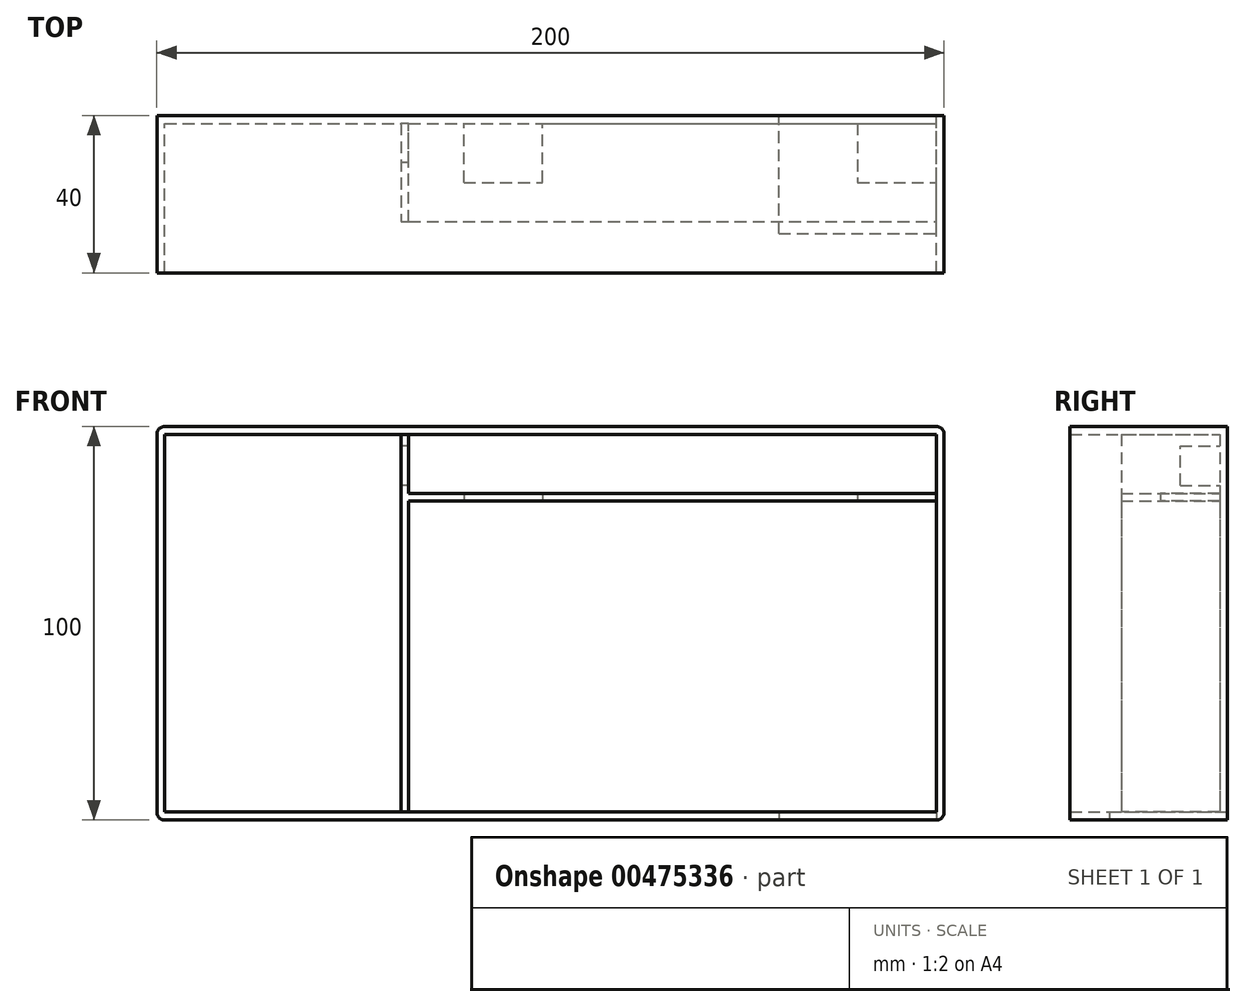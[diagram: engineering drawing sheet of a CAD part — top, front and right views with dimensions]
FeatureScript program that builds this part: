
annotation { "Feature Type Name" : "Feature", "Feature Type Description" : "" }
export const myFeature = defineFeature(function(context is Context, id is Id, definition is map)
    precondition{}
    {
        {
            var Q0;
            Q0=qCreatedBy(makeId("Front.planeOp"),FACE);
            var sketch = newSketch(context, id + "F0", { "sketchPlane" : qUnion([Q0])});
            skLineSegment(sketch, "E0.bottom", {"start": v(-123.67, 31.9) * mm, "end": v(76.33, 31.9) * mm});
            skLineSegment(sketch, "E0.top", {"start": v(-123.67, -68.1) * mm, "end": v(76.33, -68.1) * mm});
            skLineSegment(sketch, "E0.left", {"start": v(-123.67, 31.9) * mm, "end": v(-123.67, -68.1) * mm});
            skLineSegment(sketch, "E0.right", {"start": v(76.33, 31.9) * mm, "end": v(76.33, -68.1) * mm});
            skLineSegment(sketch, "E1.bottom", {"start": v(-121.67, 29.9) * mm, "end": v(74.33, 29.9) * mm});
            skLineSegment(sketch, "E1.top", {"start": v(-121.67, -66.1) * mm, "end": v(74.33, -66.1) * mm});
            skLineSegment(sketch, "E1.left", {"start": v(-121.67, 29.9) * mm, "end": v(-121.67, -66.1) * mm});
            skLineSegment(sketch, "E1.right", {"start": v(74.33, 29.9) * mm, "end": v(74.33, -66.1) * mm});
            skSolve(sketch);
        }
        {
            var Q0;
            Q0=makeQuery(id+"F0.imprint","IMPRINT",FACE,{"disambiguationData":[TD([[makeQuery(id+"F0.imprint","IMPRINT",EDGE,{"derivedFrom":sQuery(id+"F0.wireOp",EDGE,"E0.bottom")}),-1.0]])]});
            extrude(context, id + "F1", {"entities" : qUnion([Q0]), "depth" : 40 * mm});
        }
        {
            var Q0;
            Q0=makeQuery(id+"F0.imprint","IMPRINT",FACE,{"disambiguationData":[TD([[makeQuery(id+"F0.imprint","IMPRINT",EDGE,{"derivedFrom":sQuery(id+"F0.wireOp",EDGE,"E1.bottom")}),-1.0]])]});
            extrude(context, id + "F2", {"entities" : qUnion([Q0]), "operationType" : NewBodyOperationType.ADD, "depth" : 2 * mm});
        }
        {
            var Q0;
            Q0=makeQuery(id+"F2.opExtrude","CAP_FACE",FACE,{"disambiguationData":[OSD([sQuery(id+"F0.wireOp",EDGE,"E1.bottom"),sQuery(id+"F0.wireOp",EDGE,"E1.top"),sQuery(id+"F0.wireOp",EDGE,"E1.left"),sQuery(id+"F0.wireOp",EDGE,"E1.right")])],"isStart":false});
            var sketch = newSketch(context, id + "F3", { "sketchPlane" : qUnion([Q0])});
            skLineSegment(sketch, "E2.bottom", {"start": v(-121.67, 29.9) * mm, "end": v(-59.67, 29.9) * mm});
            skLineSegment(sketch, "E2.top", {"start": v(-121.67, -66.1) * mm, "end": v(-59.67, -66.1) * mm});
            skLineSegment(sketch, "E2.left", {"start": v(-121.67, 29.9) * mm, "end": v(-121.67, -66.1) * mm});
            skLineSegment(sketch, "E2.right", {"start": v(-59.67, 29.9) * mm, "end": v(-59.67, -66.1) * mm});
            skSolve(sketch);
        }
        {
            var Q0;
            Q0 = qSketchRegion(id + "F3", true);
            extrude(context, id + "F4", {"entities" : qUnion([Q0]), "operationType" : NewBodyOperationType.ADD, "depth" : 25 * mm});
        }
        {
            var Q0;
            Q0=makeQuery(id+"F4.opExtrude","CAP_FACE",FACE,{"disambiguationData":[OSD([sQuery(id+"F3.wireOp",EDGE,"E2.bottom"),sQuery(id+"F3.wireOp",EDGE,"E2.top"),sQuery(id+"F3.wireOp",EDGE,"E2.left"),sQuery(id+"F3.wireOp",EDGE,"E2.right")])],"isStart":false});
            var sketch = newSketch(context, id + "F5", { "sketchPlane" : qUnion([Q0])});
            skLineSegment(sketch, "E3.bottom", {"start": v(-121.67, 29.9) * mm, "end": v(-61.67, 29.9) * mm});
            skLineSegment(sketch, "E3.top", {"start": v(-121.67, -66.1) * mm, "end": v(-61.67, -66.1) * mm});
            skLineSegment(sketch, "E3.left", {"start": v(-121.67, 29.9) * mm, "end": v(-121.67, -66.1) * mm});
            skLineSegment(sketch, "E3.right", {"start": v(-61.67, 29.9) * mm, "end": v(-61.67, -66.1) * mm});
            skSolve(sketch);
        }
        {
            var Q0;
            Q0 = qSketchRegion(id + "F5", true);
            extrude(context, id + "F6", {"entities" : qUnion([Q0]), "operationType" : NewBodyOperationType.REMOVE, "oppositeDirection" : true, "depth" : 25 * mm});
        }
        {
            var Q0;
            Q0=makeQuery(id+"F2.opExtrude","CAP_FACE",FACE,{"disambiguationData":[OSD([sQuery(id+"F0.wireOp",EDGE,"E1.bottom"),sQuery(id+"F0.wireOp",EDGE,"E1.top"),sQuery(id+"F0.wireOp",EDGE,"E1.left"),sQuery(id+"F0.wireOp",EDGE,"E1.right")])],"isStart":false});
            var sketch = newSketch(context, id + "F7", { "sketchPlane" : qUnion([Q0])});
            skLineSegment(sketch, "E4.bottom", {"start": v(-59.67, 29.9) * mm, "end": v(-13.67, 29.9) * mm});
            skLineSegment(sketch, "E4.top", {"start": v(-59.67, 14.9) * mm, "end": v(-13.67, 14.9) * mm});
            skLineSegment(sketch, "E4.left", {"start": v(-59.67, 29.9) * mm, "end": v(-59.67, 14.9) * mm});
            skLineSegment(sketch, "E4.right", {"start": v(-13.67, 29.9) * mm, "end": v(-13.67, 14.9) * mm});
            skLineSegment(sketch, "E5.bottom", {"start": v(-61.67, 29.9) * mm, "end": v(-11.67, 29.9) * mm});
            skLineSegment(sketch, "E5.top", {"start": v(-61.67, 12.9) * mm, "end": v(-11.67, 12.9) * mm});
            skLineSegment(sketch, "E5.left", {"start": v(-61.67, 29.9) * mm, "end": v(-61.67, 12.9) * mm});
            skLineSegment(sketch, "E5.right", {"start": v(-11.67, 29.9) * mm, "end": v(-11.67, 12.9) * mm});
            skSolve(sketch);
        }
        {
            var Q0;
            Q0=makeQuery(id+"F7.imprint","IMPRINT",FACE,{"disambiguationData":[TD([[makeQuery(id+"F7.imprint","IMPRINT",EDGE,{"derivedFrom":sQuery(id+"F7.wireOp",EDGE,"E4.top")}),-1.0]])]});
            extrude(context, id + "F8", {"entities" : qUnion([Q0]), "operationType" : NewBodyOperationType.ADD, "depth" : 25 * mm});
        }
        {
            var Q0;
            Q0=makeQuery(id+"F8.opExtrude","SWEPT_FACE",FACE,{"disambiguationData":[OSD([sQuery(id+"F7.wireOp",EDGE,"E5.top")])]});
            var sketch = newSketch(context, id + "F9", { "sketchPlane" : qUnion([Q0])});
            skLineSegment(sketch, "E6.bottom", {"start": v(7.08, 2) * mm, "end": v(-6.92, 2) * mm});
            skLineSegment(sketch, "E6.top", {"start": v(7.08, 12) * mm, "end": v(-6.92, 12) * mm});
            skLineSegment(sketch, "E6.left", {"start": v(7.08, 2) * mm, "end": v(7.08, 12) * mm});
            skLineSegment(sketch, "E6.right", {"start": v(-6.92, 2) * mm, "end": v(-6.92, 12) * mm});
            skSolve(sketch);
        }
        {
            var Q0;
            Q0 = qSketchRegion(id + "F9", true);
            extrude(context, id + "F10", {"entities" : qUnion([Q0]), "operationType" : NewBodyOperationType.REMOVE, "oppositeDirection" : true, "depth" : 5 * mm});
        }
        {
            var Q0;
            Q0=makeQuery(id+"F1.opExtrude","SWEPT_FACE",FACE,{"disambiguationData":[OSD([sQuery(id+"F0.wireOp",EDGE,"E0.top")])]});
            var sketch = newSketch(context, id + "F11", { "sketchPlane" : qUnion([Q0])});
            skLineSegment(sketch, "E7.bottom", {"start": v(-43.67, 30) * mm, "end": v(-3.67, 30) * mm});
            skLineSegment(sketch, "E7.top", {"start": v(-43.67, 0) * mm, "end": v(-3.67, 0) * mm});
            skLineSegment(sketch, "E7.left", {"start": v(-43.67, 30) * mm, "end": v(-43.67, 2) * mm});
            skLineSegment(sketch, "E7.right", {"start": v(-3.67, 30) * mm, "end": v(-3.67, 2) * mm});
            skLineSegment(sketch, "E8.bottom", {"start": v(-43.67, 2) * mm, "end": v(-3.67, 2) * mm});
            skSolve(sketch);
        }
        {
            var Q0;
            Q0=makeQuery(id+"F6.boolean.opBoolean","COPY",FACE,{"derivedFrom":makeQuery(id+"F6.opExtrude","SWEPT_FACE",FACE,{"disambiguationData":[OSD([sQuery(id+"F5.wireOp",EDGE,"E3.right")])]})});
            var sketch = newSketch(context, id + "F12", { "sketchPlane" : qUnion([Q0])});
            skLineSegment(sketch, "E9.bottom", {"start": v(2, 26.9) * mm, "end": v(12, 26.9) * mm});
            skLineSegment(sketch, "E9.top", {"start": v(2, 16.9) * mm, "end": v(12, 16.9) * mm});
            skLineSegment(sketch, "E9.left", {"start": v(2, 26.9) * mm, "end": v(2, 16.9) * mm});
            skLineSegment(sketch, "E9.right", {"start": v(12, 26.9) * mm, "end": v(12, 16.9) * mm});
            skSolve(sketch);
        }
        {
            var Q0;
            Q0 = qSketchRegion(id + "F12", true);
            extrude(context, id + "F13", {"entities" : qUnion([Q0]), "operationType" : NewBodyOperationType.REMOVE, "oppositeDirection" : true, "depth" : 5 * mm});
        }
        {
            var Q0;
            Q0=makeQuery(id+"F1.opExtrude","SWEPT_EDGE",EDGE,{"disambiguationData":[OSD([sQuery(id+"F0.wireOp",EDGE,"E0.top"),sQuery(id+"F0.wireOp",EDGE,"E0.right")])]});
            var Q1;
            Q1=makeQuery(id+"F1.opExtrude","SWEPT_EDGE",EDGE,{"disambiguationData":[OSD([sQuery(id+"F0.wireOp",EDGE,"E0.bottom"),sQuery(id+"F0.wireOp",EDGE,"E0.right")])]});
            var Q2;
            Q2=makeQuery(id+"F1.opExtrude","SWEPT_EDGE",EDGE,{"disambiguationData":[OSD([sQuery(id+"F0.wireOp",EDGE,"E0.top"),sQuery(id+"F0.wireOp",EDGE,"E0.left")])]});
            var Q3;
            Q3=makeQuery(id+"F1.opExtrude","SWEPT_EDGE",EDGE,{"disambiguationData":[OSD([sQuery(id+"F0.wireOp",EDGE,"E0.bottom"),sQuery(id+"F0.wireOp",EDGE,"E0.left")])]});
            fillet(context, id + "F14", {"entities" : qUnion([Q0, Q1, Q2, Q3]), "radius" : 2 * mm, "tangentPropagation" : true, "allowEdgeOverflow" : false});
        }
        {
            var Q0;
            Q0=makeQuery(id+"F8.opExtrude","SWEPT_FACE",FACE,{"disambiguationData":[OSD([sQuery(id+"F7.wireOp",EDGE,"E5.top")])]});
            var sketch = newSketch(context, id + "F15", { "sketchPlane" : qUnion([Q0])});
            skLineSegment(sketch, "E10.bottom", {"start": v(-45.67, 17) * mm, "end": v(-25.67, 17) * mm});
            skLineSegment(sketch, "E10.top", {"start": v(-45.67, 2) * mm, "end": v(-25.67, 2) * mm});
            skLineSegment(sketch, "E10.left", {"start": v(-45.67, 17) * mm, "end": v(-45.67, 2) * mm});
            skLineSegment(sketch, "E10.right", {"start": v(-25.67, 17) * mm, "end": v(-25.67, 2) * mm});
            skSolve(sketch);
        }
        {
            var Q0;
            Q0=makeQuery(id+"F15.imprint","IMPRINT",FACE,{"disambiguationData":[TD([[makeQuery(id+"F15.imprint","IMPRINT",EDGE,{"derivedFrom":sQuery(id+"F15.wireOp",EDGE,"E10.bottom")}),-1.0]])]});
            extrude(context, id + "F16", {"entities" : qUnion([Q0]), "operationType" : NewBodyOperationType.REMOVE, "oppositeDirection" : true, "depth" : 2 * mm});
        }
        {
            var Q0;
            Q0=makeQuery(id+"F8.opExtrude","SWEPT_FACE",FACE,{"disambiguationData":[OSD([sQuery(id+"F7.wireOp",EDGE,"E5.right")])]});
            var sketch = newSketch(context, id + "F17", { "sketchPlane" : qUnion([Q0])});
            skLineSegment(sketch, "E11.bottom", {"start": v(-2, 16.4) * mm, "end": v(-17, 16.4) * mm});
            skLineSegment(sketch, "E11.top", {"start": v(-2, 26.4) * mm, "end": v(-17, 26.4) * mm});
            skLineSegment(sketch, "E11.left", {"start": v(-2, 16.4) * mm, "end": v(-2, 26.4) * mm});
            skLineSegment(sketch, "E11.right", {"start": v(-17, 16.4) * mm, "end": v(-17, 26.4) * mm});
            skSolve(sketch);
        }
        {
            var Q0;
            Q0 = qSketchRegion(id + "F17", true);
            extrude(context, id + "F18", {"entities" : qUnion([Q0]), "operationType" : NewBodyOperationType.REMOVE, "oppositeDirection" : true, "depth" : 2 * mm});
        }
        {
            var Q0;
            {var subQ1=sQuery(id+"F5.wireOp",EDGE,"E3.bottom");var subQ3=sQuery(id+"F0.wireOp",EDGE,"E1.right");var subQ4=sQuery(id+"F0.wireOp",EDGE,"E1.top");var subQ5=sQuery(id+"F0.wireOp",EDGE,"E1.bottom");var subQ7=sQuery(id+"F5.wireOp",EDGE,"E3.top");var subQ8=makeQuery(id+"F2.opExtrude","CAP_FACE",FACE,{"disambiguationData":[OSD([subQ5,subQ4,sQuery(id+"F0.wireOp",EDGE,"E1.left"),subQ3])],"isStart":false});Q0=makeQuery(id+"F18.boolean.opBoolean","MERGE",FACE,{"derivedFrom":[makeQuery(id+"F16.boolean.opBoolean","MERGE",FACE,{"derivedFrom":[makeQuery(id+"F13.boolean.opBoolean","MERGE",FACE,{"derivedFrom":[makeQuery(id+"F6.boolean.opBoolean","COPY",FACE,{"derivedFrom":makeQuery(id+"F6.opExtrude","CAP_FACE",FACE,{"disambiguationData":[OSD([subQ1,subQ7,sQuery(id+"F5.wireOp",EDGE,"E3.left"),sQuery(id+"F5.wireOp",EDGE,"E3.right")])],"isStart":false})}),makeQuery(id+"F8.boolean.opBoolean","SPLIT",FACE,{"disambiguationData":[TD([makeQuery(id+"F8.opExtrude","SWEPT_FACE",FACE,{"disambiguationData":[OSD([sQuery(id+"F7.wireOp",EDGE,"E4.top")])]})])],"derivedFrom":subQ8}),makeQuery(id+"F13.opExtrude","SWEPT_FACE",FACE,{"disambiguationData":[OSD([sQuery(id+"F12.wireOp",EDGE,"E9.left")])]})]}),makeQuery(id+"FwYcfOTWCvAisjY_1.boolean.opBoolean","MERGE",FACE,{"derivedFrom":[makeQuery(id+"F8.boolean.opBoolean","SPLIT",FACE,{"disambiguationData":[TD([makeQuery(id+"F1.opExtrude","SWEPT_FACE",FACE,{"disambiguationData":[OSD([subQ4])]})])],"derivedFrom":subQ8}),makeQuery(id+"FwYcfOTWCvAisjY_1.opExtrude","SWEPT_FACE",FACE,{"disambiguationData":[OSD([sQuery(id+"F11.wireOp",EDGE,"E8.bottom")])]})]}),makeQuery(id+"F16.opExtrude","SWEPT_FACE",FACE,{"disambiguationData":[OSD([sQuery(id+"F15.wireOp",EDGE,"E10.top")])]})]}),makeQuery(id+"F18.opExtrude","SWEPT_FACE",FACE,{"disambiguationData":[OSD([sQuery(id+"F17.wireOp",EDGE,"E11.left")])]})]});}
            var sketch = newSketch(context, id + "F19", { "sketchPlane" : qUnion([Q0])});
            skLineSegment(sketch, "E12.bottom", {"start": v(-11.67, 12.9) * mm, "end": v(74.33, 12.9) * mm});
            skLineSegment(sketch, "E12.top", {"start": v(-11.67, 29.9) * mm, "end": v(74.33, 29.9) * mm});
            skLineSegment(sketch, "E12.left", {"start": v(-11.67, 12.9) * mm, "end": v(-11.67, 29.9) * mm});
            skLineSegment(sketch, "E12.right", {"start": v(74.33, 12.9) * mm, "end": v(74.33, 29.9) * mm});
            skLineSegment(sketch, "E13.bottom", {"start": v(-11.67, 14.9) * mm, "end": v(74.33, 14.9) * mm});
            skLineSegment(sketch, "E13.top", {"start": v(-11.67, 27.9) * mm, "end": v(74.33, 27.9) * mm});
            skLineSegment(sketch, "E13.left", {"start": v(-11.67, 14.9) * mm, "end": v(-11.67, 27.9) * mm});
            skLineSegment(sketch, "E13.right", {"start": v(74.33, 14.9) * mm, "end": v(74.33, 27.9) * mm});
            skSolve(sketch);
        }
        {
            var Q0;
            {var subQ0=sQuery(id+"F19.wireOp",EDGE,"E12.bottom");Q0=makeQuery(id+"F19.imprint","IMPRINT",FACE,{"disambiguationData":[TD([[makeQuery(id+"F19.imprint","IMPRINT",EDGE,{"derivedFrom":subQ0}),1.0]])]});}
            var Q1;
            {var subQ0=sQuery(id+"F19.wireOp",EDGE,"E12.top");Q1=makeQuery(id+"F19.imprint","IMPRINT",FACE,{"disambiguationData":[TD([[makeQuery(id+"F19.imprint","IMPRINT",EDGE,{"derivedFrom":subQ0}),-1.0]])]});}
            extrude(context, id + "F20", {"entities" : qUnion([Q0, Q1]), "operationType" : NewBodyOperationType.ADD, "depth" : 25 * mm});
        }
        {
            var Q0;
            Q0=makeQuery(id+"F8.opExtrude","SWEPT_FACE",FACE,{"disambiguationData":[OSD([sQuery(id+"F7.wireOp",EDGE,"E4.right")])]});
            var sketch = newSketch(context, id + "F21", { "sketchPlane" : qUnion([Q0])});
            skLineSegment(sketch, "E14.bottom", {"start": v(2, 29.9) * mm, "end": v(27, 29.9) * mm});
            skLineSegment(sketch, "E14.top", {"start": v(2, 14.9) * mm, "end": v(27, 14.9) * mm});
            skLineSegment(sketch, "E14.left", {"start": v(2, 29.9) * mm, "end": v(2, 14.9) * mm});
            skLineSegment(sketch, "E14.right", {"start": v(27, 29.9) * mm, "end": v(27, 14.9) * mm});
            skSolve(sketch);
        }
        {
            var Q0;
            Q0 = qSketchRegion(id + "F21", true);
            extrude(context, id + "F22", {"entities" : qUnion([Q0]), "operationType" : NewBodyOperationType.REMOVE, "oppositeDirection" : true, "depth" : 88 * mm});
        }
        {
            var Q0;
            Q0=makeQuery(id+"F1.opExtrude","SWEPT_FACE",FACE,{"disambiguationData":[OSD([sQuery(id+"F0.wireOp",EDGE,"E0.top")])]});
            var sketch = newSketch(context, id + "F23", { "sketchPlane" : qUnion([Q0])});
            skLineSegment(sketch, "E15.bottom", {"start": v(34.33, 30) * mm, "end": v(74.33, 30) * mm});
            skLineSegment(sketch, "E15.top", {"start": v(34.33, 0) * mm, "end": v(74.33, 0) * mm});
            skLineSegment(sketch, "E15.left", {"start": v(34.33, 30) * mm, "end": v(34.33, 0) * mm});
            skLineSegment(sketch, "E15.right", {"start": v(74.33, 30) * mm, "end": v(74.33, 0) * mm});
            skSolve(sketch);
        }
        {
            var Q0;
            Q0 = qSketchRegion(id + "F23", true);
            extrude(context, id + "F24", {"entities" : qUnion([Q0]), "operationType" : NewBodyOperationType.REMOVE, "oppositeDirection" : true, "depth" : 2 * mm});
        }
        {
            var Q0;
            Q0=makeQuery(id+"F20.boolean.opBoolean","MERGE",FACE,{"derivedFrom":[makeQuery(id+"F8.opExtrude","SWEPT_FACE",FACE,{"disambiguationData":[OSD([sQuery(id+"F7.wireOp",EDGE,"E5.top")])]}),makeQuery(id+"F20.opExtrude","SWEPT_FACE",FACE,{"disambiguationData":[OSD([sQuery(id+"F19.wireOp",EDGE,"E12.bottom")])]})]});
            var sketch = newSketch(context, id + "F25", { "sketchPlane" : qUnion([Q0])});
            skLineSegment(sketch, "E16.bottom", {"start": v(54.33, 2) * mm, "end": v(74.33, 2) * mm});
            skLineSegment(sketch, "E16.top", {"start": v(54.33, 17) * mm, "end": v(74.33, 17) * mm});
            skLineSegment(sketch, "E16.left", {"start": v(54.33, 2) * mm, "end": v(54.33, 17) * mm});
            skLineSegment(sketch, "E16.right", {"start": v(74.33, 2) * mm, "end": v(74.33, 17) * mm});
            skSolve(sketch);
        }
        {
            var Q0;
            Q0 = qSketchRegion(id + "F25", true);
            extrude(context, id + "F26", {"entities" : qUnion([Q0]), "operationType" : NewBodyOperationType.REMOVE, "oppositeDirection" : true, "depth" : 2 * mm});
        }
    });
